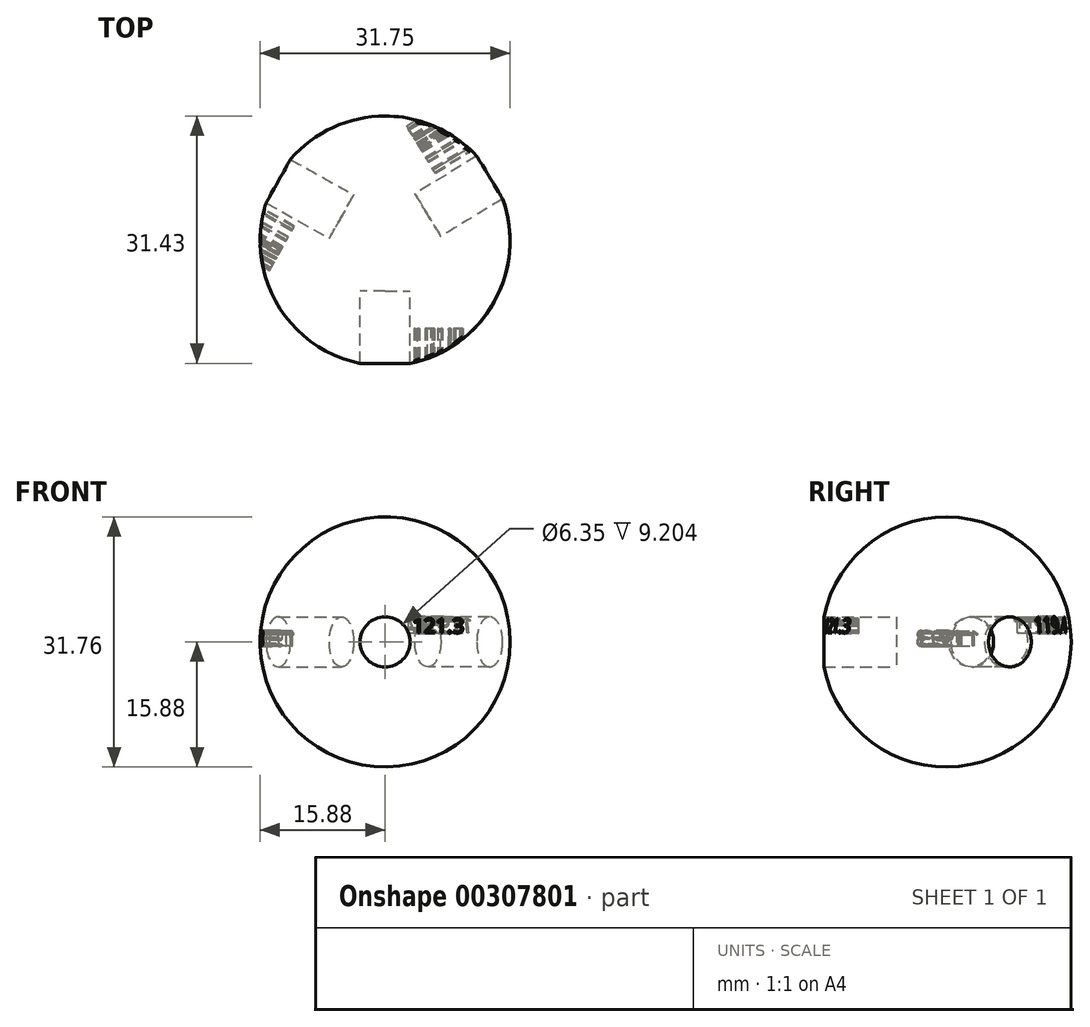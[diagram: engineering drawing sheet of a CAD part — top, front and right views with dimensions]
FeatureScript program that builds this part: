
annotation { "Feature Type Name" : "Feature", "Feature Type Description" : "" }
export const myFeature = defineFeature(function(context is Context, id is Id, definition is map)
    precondition{}
    {
        {
            var Q0;
            Q0=qCreatedBy(makeId("Top.planeOp"),FACE);
            var sketch = newSketch(context, id + "F0", { "sketchPlane" : qUnion([Q0])});
            skArc(sketch, "E0", {"start": v(0, 15.88) * mm, "mid": v(-15.88, 0) * mm, "end": v(0, -15.88) * mm});
            skLineSegment(sketch, "E1", {"start": v(0, 15.88) * mm, "end": v(0, -15.88) * mm});
            skSolve(sketch);
        }
        {
            var Q0;
            Q0=makeQuery(id+"F0.imprint","IMPRINT",FACE,{"disambiguationData":[TD([[makeQuery(id+"F0.imprint","IMPRINT",EDGE,{"derivedFrom":sQuery(id+"F0.wireOp",EDGE,"E0")}),1.0]])]});
            var Q1;
            Q1=sQuery(id+"F0.wireOp",EDGE,"E1");
            revolve(context, id + "F1", {"entities" : qUnion([Q0]), "axis" : qUnion([Q1]), "revolveType" : RevolveType.FULL});
        }
        {
            var Q0;
            Q0=qCreatedBy(makeId("Front.planeOp"),FACE);
            var sketch = newSketch(context, id + "F2", { "sketchPlane" : qUnion([Q0])});
            skLineSegment(sketch, "E2", {"start": v(0, 0) * mm, "end": v(0, 75.26) * mm, "construction": true});
            skSolve(sketch);
        }
        {
            var Q0;
            Q0=qCreatedBy(makeId("Front.planeOp"),FACE);
            cPlane(context, id + "F3", {"entities" : qUnion([Q0]), "cplaneType" : CPlaneType.OFFSET, "offset" : 6.35 * mm, "width" : 152.4 * mm, "height" : 152.4 * mm});
        }
        {
            var Q0;
            Q0=qCreatedBy(id+"F3.planeOp",FACE);
            var sketch = newSketch(context, id + "F4", { "sketchPlane" : qUnion([Q0])});
            skCircle(sketch, "E3", {"center": v(0, 0) * mm, "radius": 3.18 * mm});
            skSolve(sketch);
        }
        {
            var Q0;
            Q0 = qSketchRegion(id + "F4", true);
            extrude(context, id + "F5", {"entities" : qUnion([Q0]), "depth" : 25.4 * mm});
        }
        {
            var Q0;
            Q0=makeQuery(id+"F5.opExtrude","SWEPT_BODY",BODY,{"disambiguationData":[OSD([sQuery(id+"F4.wireOp",EDGE,"E3")])]});
            var Q1;
            Q1=sQuery(id+"F2.wireOp",EDGE,"E2");
            var Q2;
            Q2=sQuery(id+"F2.wireOp",EDGE,"E2");
            transform(context, id + "F6", {"entities" : qUnion([Q0]), "transformType" : TransformType.ROTATION, "transformAxis" : qUnion([Q2]), "angle" : 119.3 * degree, "oppositeDirection" : true, "makeCopy" : true});
        }
        {
            var Q0;
            Q0=makeQuery(id+"F6.opPattern","COPY",BODY,{"derivedFrom":makeQuery(id+"F5.opExtrude","SWEPT_BODY",BODY,{"disambiguationData":[OSD([sQuery(id+"F4.wireOp",EDGE,"E3")])]}),"instanceName":"1"});
            var Q1;
            Q1=sQuery(id+"F2.wireOp",EDGE,"E2");
            transform(context, id + "F7", {"entities" : qUnion([Q0]), "transformType" : TransformType.ROTATION, "transformAxis" : qUnion([Q1]), "angle" : 119.4 * degree, "oppositeDirection" : true, "makeCopy" : true});
        }
        {
            var Q0;
            Q0=makeQuery(id+"F7.opPattern","COPY",FACE,{"derivedFrom":makeQuery(id+"F6.opPattern","COPY",FACE,{"derivedFrom":makeQuery(id+"F5.opExtrude","CAP_FACE",FACE,{"disambiguationData":[OSD([sQuery(id+"F4.wireOp",EDGE,"E3")])],"isStart":false}),"instanceName":"1"}),"instanceName":"1"});
            cPlane(context, id + "F8", {"entities" : qUnion([Q0]), "cplaneType" : CPlaneType.OFFSET, "offset" : 12.7 * mm, "oppositeDirection" : true, "width" : 152.4 * mm, "height" : 152.4 * mm});
        }
        {
            var Q0;
            Q0=qCreatedBy(id+"F8.planeOp",FACE);
            var sketch = newSketch(context, id + "F9", { "sketchPlane" : qUnion([Q0])});
            skText(sketch, "E4", { "text": "119.4", "fontName": "OpenSans-Regular.ttf"});
            const initialGuessF9  = {"E4": [0.0038, 0.00113, 1, 0, 0.00207]};
            skSetInitialGuess(sketch, initialGuessF9);
            skSolve(sketch);
        }
        {
            var Q0;
            Q0 = qSketchRegion(id + "F9", true);
            extrude(context, id + "F10", {"entities" : qUnion([Q0]), "operationType" : NewBodyOperationType.REMOVE, "oppositeDirection" : true, "depth" : 9.12 * mm});
        }
        {
            var Q0;
            Q0=makeQuery(id+"F6.opPattern","COPY",FACE,{"derivedFrom":makeQuery(id+"F5.opExtrude","CAP_FACE",FACE,{"disambiguationData":[OSD([sQuery(id+"F4.wireOp",EDGE,"E3")])],"isStart":false}),"instanceName":"1"});
            cPlane(context, id + "F11", {"entities" : qUnion([Q0]), "cplaneType" : CPlaneType.OFFSET, "offset" : 12.7 * mm, "oppositeDirection" : true, "width" : 152.4 * mm, "height" : 152.4 * mm});
        }
        {
            var Q0;
            Q0=qCreatedBy(id+"F11.planeOp",FACE);
            var sketch = newSketch(context, id + "F12", { "sketchPlane" : qUnion([Q0])});
            skText(sketch, "E5", { "text": "119.3", "fontName": "OpenSans-Regular.ttf"});
            const initialGuessF12  = {"E5": [0.00375, -0.00052, 1, 0, 0.00194]};
            skSetInitialGuess(sketch, initialGuessF12);
            skSolve(sketch);
        }
        {
            var Q0;
            Q0 = qSketchRegion(id + "F12", true);
            extrude(context, id + "F13", {"entities" : qUnion([Q0]), "operationType" : NewBodyOperationType.REMOVE, "oppositeDirection" : true, "depth" : 8.05 * mm});
        }
        {
            var Q0;
            Q0=makeQuery(id+"F6.opPattern","COPY",BODY,{"derivedFrom":makeQuery(id+"F5.opExtrude","SWEPT_BODY",BODY,{"disambiguationData":[OSD([sQuery(id+"F4.wireOp",EDGE,"E3")])]}),"instanceName":"1"});
            var Q1;
            Q1=makeQuery(id+"F5.opExtrude","SWEPT_BODY",BODY,{"disambiguationData":[OSD([sQuery(id+"F4.wireOp",EDGE,"E3")])]});
            var Q2;
            Q2=makeQuery(id+"F7.opPattern","COPY",BODY,{"derivedFrom":makeQuery(id+"F6.opPattern","COPY",BODY,{"derivedFrom":makeQuery(id+"F5.opExtrude","SWEPT_BODY",BODY,{"disambiguationData":[OSD([sQuery(id+"F4.wireOp",EDGE,"E3")])]}),"instanceName":"1"}),"instanceName":"1"});
            var Q3;
            Q3=makeQuery(id+"F1.opRevolve","SWEPT_BODY",BODY,{"disambiguationData":[OSD([sQuery(id+"F0.wireOp",EDGE,"E0"),sQuery(id+"F0.wireOp",EDGE,"E1")])]});
            booleanBodies(context, id + "F14", {"operationType" : BooleanOperationType.SUBTRACTION, "tools" : qUnion([Q0, Q1, Q2]), "targets" : qUnion([Q3])});
        }
        {
            var Q0;
            Q0=makeQuery(id+"F4.imprint","IMPRINT",FACE,{"disambiguationData":[TD([[makeQuery(id+"F4.imprint","IMPRINT",EDGE,{"derivedFrom":sQuery(id+"F4.wireOp",EDGE,"E3")}),1.0]])]});
            cPlane(context, id + "F15", {"entities" : qUnion([Q0]), "cplaneType" : CPlaneType.OFFSET, "offset" : 13.33 * mm, "width" : 152.4 * mm, "height" : 152.4 * mm});
        }
        {
            var Q0;
            Q0=qCreatedBy(id+"F15.planeOp",FACE);
            var sketch = newSketch(context, id + "F16", { "sketchPlane" : qUnion([Q0])});
            skText(sketch, "E6", { "text": "121.3", "fontName": "OpenSans-Regular.ttf"});
            const initialGuessF16  = {"E6": [0.00346, 0.00113, 1, 0, 0.00185]};
            skSetInitialGuess(sketch, initialGuessF16);
            skSolve(sketch);
        }
        {
            var Q0;
            Q0 = qSketchRegion(id + "F16", true);
            extrude(context, id + "F17", {"entities" : qUnion([Q0]), "operationType" : NewBodyOperationType.REMOVE, "oppositeDirection" : true, "depth" : 8.53 * mm});
        }
    });
